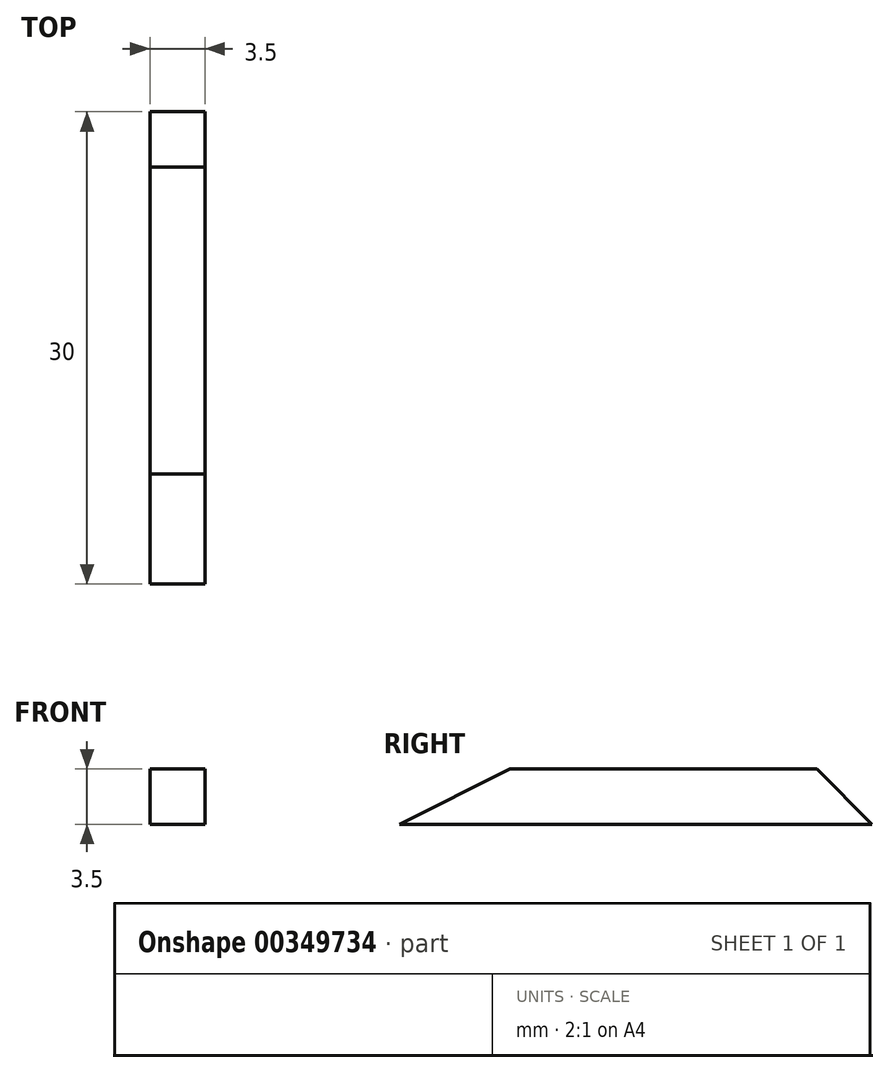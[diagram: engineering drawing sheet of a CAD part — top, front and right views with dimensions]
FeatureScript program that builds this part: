
annotation { "Feature Type Name" : "Feature", "Feature Type Description" : "" }
export const myFeature = defineFeature(function(context is Context, id is Id, definition is map)
    precondition{}
    {
        {
            var Q0;
            Q0=qCreatedBy(makeId("Top.planeOp"),FACE);
            var sketch = newSketch(context, id + "F0", { "sketchPlane" : qUnion([Q0])});
            skLineSegment(sketch, "E0.bottom", {"start": v(-1.75, 15) * mm, "end": v(1.75, 15) * mm});
            skLineSegment(sketch, "E0.top", {"start": v(-1.75, -15) * mm, "end": v(1.75, -15) * mm});
            skLineSegment(sketch, "E0.left", {"start": v(-1.75, 15) * mm, "end": v(-1.75, -15) * mm});
            skLineSegment(sketch, "E0.right", {"start": v(1.75, 15) * mm, "end": v(1.75, -15) * mm});
            skPoint(sketch, "E0.middle", {"position": v(0, 0) * mm});
            skSolve(sketch);
        }
        {
            var Q0;
            Q0=qSketchRegion(id+"F0",true);
            extrude(context, id + "F1", {"entities" : qUnion([Q0]), "depth" : 3.5 * mm});
        }
        {
            var Q0;
            Q0=makeQuery(id+"F1.opExtrude","SWEPT_FACE",FACE,{"disambiguationData":[OSD([sQuery(id+"F0.wireOp",EDGE,"E0.right")])]});
            var sketch = newSketch(context, id + "F2", { "sketchPlane" : qUnion([Q0])});
            skLineSegment(sketch, "E1", {"start": v(-15, 0) * mm, "end": v(-8, 3.5) * mm});
            skLineSegment(sketch, "E2", {"start": v(-15, 0) * mm, "end": v(-15, 3.5) * mm});
            skLineSegment(sketch, "E3", {"start": v(-15, 3.5) * mm, "end": v(-8, 3.5) * mm});
            skLineSegment(sketch, "E4", {"start": v(11.5, 3.5) * mm, "end": v(15, 0) * mm});
            skLineSegment(sketch, "E5", {"start": v(15, 0) * mm, "end": v(15, 3.5) * mm});
            skLineSegment(sketch, "E6", {"start": v(15, 3.5) * mm, "end": v(11.5, 3.5) * mm});
            skSolve(sketch);
        }
        {
            var Q0;
            Q0=qSketchRegion(id+"F2",true);
            extrude(context, id + "F3", {"entities" : qUnion([Q0]), "operationType" : NewBodyOperationType.REMOVE, "endBound" : BoundingType.THROUGH_ALL, "oppositeDirection" : true, "depth" : 25.4 * mm});
        }
    });
